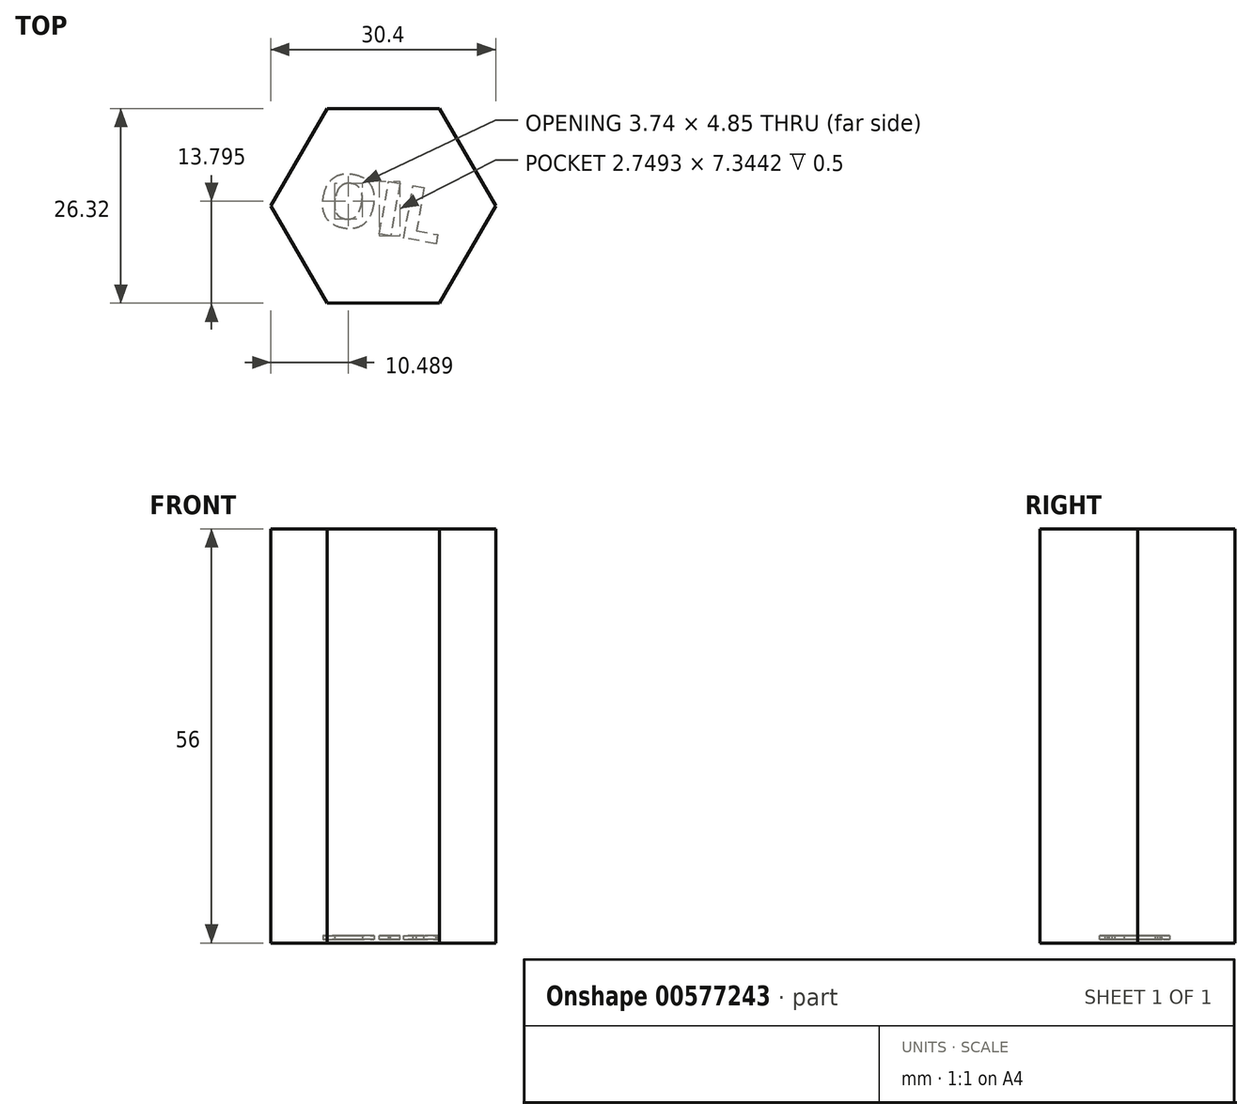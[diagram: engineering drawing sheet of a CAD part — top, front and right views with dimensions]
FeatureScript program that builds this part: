
annotation { "Feature Type Name" : "Feature", "Feature Type Description" : "" }
export const myFeature = defineFeature(function(context is Context, id is Id, definition is map)
    precondition{}
    {
        {
            var Q0;
            Q0=qCreatedBy(makeId("Top.planeOp"),FACE);
            var sketch = newSketch(context, id + "F0", { "sketchPlane" : qUnion([Q0])});
            skCircle(sketch, "E0.cCircle", {"center": v(0, 0) * mm, "radius": 15.2 * mm, "construction": true});
            skLineSegment(sketch, "E0.0", {"start": v(15.2, 0) * mm, "end": v(7.6, -13.16) * mm});
            skLineSegment(sketch, "E0.1", {"start": v(7.6, -13.16) * mm, "end": v(-7.6, -13.16) * mm});
            skLineSegment(sketch, "E0.2", {"start": v(-7.6, -13.16) * mm, "end": v(-15.2, 0) * mm});
            skLineSegment(sketch, "E0.3", {"start": v(-15.2, 0) * mm, "end": v(-7.6, 13.16) * mm});
            skLineSegment(sketch, "E0.4", {"start": v(-7.6, 13.16) * mm, "end": v(7.6, 13.16) * mm});
            skLineSegment(sketch, "E0.5", {"start": v(7.6, 13.16) * mm, "end": v(15.2, 0) * mm});
            skSolve(sketch);
        }
        {
            var Q0;
            Q0=makeQuery(id+"F0.imprint","IMPRINT",FACE,{"disambiguationData":[TD([[makeQuery(id+"F0.imprint","IMPRINT",EDGE,{"derivedFrom":sQuery(id+"F0.wireOp",EDGE,"E0.0")}),-1.0]])]});
            extrude(context, id + "F1", {"entities" : qUnion([Q0]), "depth" : 56 * mm, "offsetDistance" : 25 * mm});
        }
        {
            var Q0;
            Q0=makeQuery(id+"F0.imprint","IMPRINT",FACE,{"disambiguationData":[TD([[makeQuery(id+"F0.imprint","IMPRINT",EDGE,{"derivedFrom":sQuery(id+"F0.wireOp",EDGE,"E0.0")}),-1.0]])]});
            var sketch = newSketch(context, id + "F2", { "sketchPlane" : qUnion([Q0])});
            skText(sketch, "E1", { "text": "OIL", "fontName": "OpenSans-Bold.ttf"});
            const initialGuessF2  = {"E1": [-0.00928, -0.00222, 0.98482, -0.17358, 0.00725]};
            skSetInitialGuess(sketch, initialGuessF2);
            skSolve(sketch);
        }
        {
            var Q0;
            Q0 = qSketchRegion(id + "F2", true);
            extrude(context, id + "F3", {"entities" : qUnion([Q0]), "oppositeDirection" : true, "depth" : 0.5 * mm, "offsetDistance" : 25 * mm});
        }
        {
            var Q0;
            Q0=qCreatedBy(makeId("Right.planeOp"),FACE);
            var sketch = newSketch(context, id + "F4", { "sketchPlane" : qUnion([Q0])});
            skLineSegment(sketch, "E2", {"start": v(0, 0) * mm, "end": v(0, 16.05) * mm, "construction": true});
            skSolve(sketch);
        }
        {
            var Q0;
            Q0=makeQuery(id+"F3.opExtrude","SWEPT_BODY",BODY,{"disambiguationData":[OSD([sQuery(id+"F2.wireOp",EDGE,"E1.sketch_text.stroke-0"),sQuery(id+"F2.wireOp",EDGE,"E1.sketch_text.stroke-1"),sQuery(id+"F2.wireOp",EDGE,"E1.sketch_text.stroke-2"),sQuery(id+"F2.wireOp",EDGE,"E1.sketch_text.stroke-3"),sQuery(id+"F2.wireOp",EDGE,"E1.sketch_text.stroke-4"),sQuery(id+"F2.wireOp",EDGE,"E1.sketch_text.stroke-5"),sQuery(id+"F2.wireOp",EDGE,"E1.sketch_text.stroke-6"),sQuery(id+"F2.wireOp",EDGE,"E1.sketch_text.stroke-7"),sQuery(id+"F2.wireOp",EDGE,"E1.sketch_text.stroke-8"),sQuery(id+"F2.wireOp",EDGE,"E1.sketch_text.stroke-9"),sQuery(id+"F2.wireOp",EDGE,"E1.sketch_text.stroke-10"),sQuery(id+"F2.wireOp",EDGE,"E1.sketch_text.stroke-11"),sQuery(id+"F2.wireOp",EDGE,"E1.sketch_text.stroke-12"),sQuery(id+"F2.wireOp",EDGE,"E1.sketch_text.stroke-13")])]});
            var Q1;
            Q1=makeQuery(id+"F3.opExtrude","SWEPT_BODY",BODY,{"disambiguationData":[OSD([sQuery(id+"F2.wireOp",EDGE,"E1.sketch_text.stroke-14"),sQuery(id+"F2.wireOp",EDGE,"E1.sketch_text.stroke-15"),sQuery(id+"F2.wireOp",EDGE,"E1.sketch_text.stroke-16"),sQuery(id+"F2.wireOp",EDGE,"E1.sketch_text.stroke-17")])]});
            var Q2;
            Q2=makeQuery(id+"F3.opExtrude","SWEPT_BODY",BODY,{"disambiguationData":[OSD([sQuery(id+"F2.wireOp",EDGE,"E1.sketch_text.stroke-18"),sQuery(id+"F2.wireOp",EDGE,"E1.sketch_text.stroke-19"),sQuery(id+"F2.wireOp",EDGE,"E1.sketch_text.stroke-20"),sQuery(id+"F2.wireOp",EDGE,"E1.sketch_text.stroke-21"),sQuery(id+"F2.wireOp",EDGE,"E1.sketch_text.stroke-22"),sQuery(id+"F2.wireOp",EDGE,"E1.sketch_text.stroke-23")])]});
            var Q3;
            Q3=sQuery(id+"F4.wireOp",EDGE,"E2");
            transform(context, id + "F5", {"entities" : qUnion([Q0, Q1, Q2]), "transformType" : TransformType.TRANSLATION_DISTANCE, "transformDirection" : qUnion([Q3]), "distance" : 1 * mm, "makeCopy" : false});
        }
        {
            var Q0;
            Q0=makeQuery(id+"F3.opExtrude","SWEPT_BODY",BODY,{"disambiguationData":[OSD([sQuery(id+"F2.wireOp",EDGE,"E1.sketch_text.stroke-0"),sQuery(id+"F2.wireOp",EDGE,"E1.sketch_text.stroke-1"),sQuery(id+"F2.wireOp",EDGE,"E1.sketch_text.stroke-2"),sQuery(id+"F2.wireOp",EDGE,"E1.sketch_text.stroke-3"),sQuery(id+"F2.wireOp",EDGE,"E1.sketch_text.stroke-4"),sQuery(id+"F2.wireOp",EDGE,"E1.sketch_text.stroke-5"),sQuery(id+"F2.wireOp",EDGE,"E1.sketch_text.stroke-6"),sQuery(id+"F2.wireOp",EDGE,"E1.sketch_text.stroke-7"),sQuery(id+"F2.wireOp",EDGE,"E1.sketch_text.stroke-8"),sQuery(id+"F2.wireOp",EDGE,"E1.sketch_text.stroke-9"),sQuery(id+"F2.wireOp",EDGE,"E1.sketch_text.stroke-10"),sQuery(id+"F2.wireOp",EDGE,"E1.sketch_text.stroke-11"),sQuery(id+"F2.wireOp",EDGE,"E1.sketch_text.stroke-12"),sQuery(id+"F2.wireOp",EDGE,"E1.sketch_text.stroke-13")])]});
            var Q1;
            Q1=makeQuery(id+"F3.opExtrude","SWEPT_BODY",BODY,{"disambiguationData":[OSD([sQuery(id+"F2.wireOp",EDGE,"E1.sketch_text.stroke-14"),sQuery(id+"F2.wireOp",EDGE,"E1.sketch_text.stroke-15"),sQuery(id+"F2.wireOp",EDGE,"E1.sketch_text.stroke-16"),sQuery(id+"F2.wireOp",EDGE,"E1.sketch_text.stroke-17")])]});
            var Q2;
            Q2=makeQuery(id+"F3.opExtrude","SWEPT_BODY",BODY,{"disambiguationData":[OSD([sQuery(id+"F2.wireOp",EDGE,"E1.sketch_text.stroke-18"),sQuery(id+"F2.wireOp",EDGE,"E1.sketch_text.stroke-19"),sQuery(id+"F2.wireOp",EDGE,"E1.sketch_text.stroke-20"),sQuery(id+"F2.wireOp",EDGE,"E1.sketch_text.stroke-21"),sQuery(id+"F2.wireOp",EDGE,"E1.sketch_text.stroke-22"),sQuery(id+"F2.wireOp",EDGE,"E1.sketch_text.stroke-23")])]});
            var Q3;
            Q3=makeQuery(id+"F1.opExtrude","SWEPT_BODY",BODY,{"disambiguationData":[OSD([sQuery(id+"F0.wireOp",EDGE,"E0.0"),sQuery(id+"F0.wireOp",EDGE,"E0.1"),sQuery(id+"F0.wireOp",EDGE,"E0.2"),sQuery(id+"F0.wireOp",EDGE,"E0.3"),sQuery(id+"F0.wireOp",EDGE,"E0.4"),sQuery(id+"F0.wireOp",EDGE,"E0.5")])]});
            booleanBodies(context, id + "F6", {"operationType" : BooleanOperationType.SUBTRACTION, "tools" : qUnion([Q0, Q1, Q2]), "targets" : qUnion([Q3])});
        }
    });
